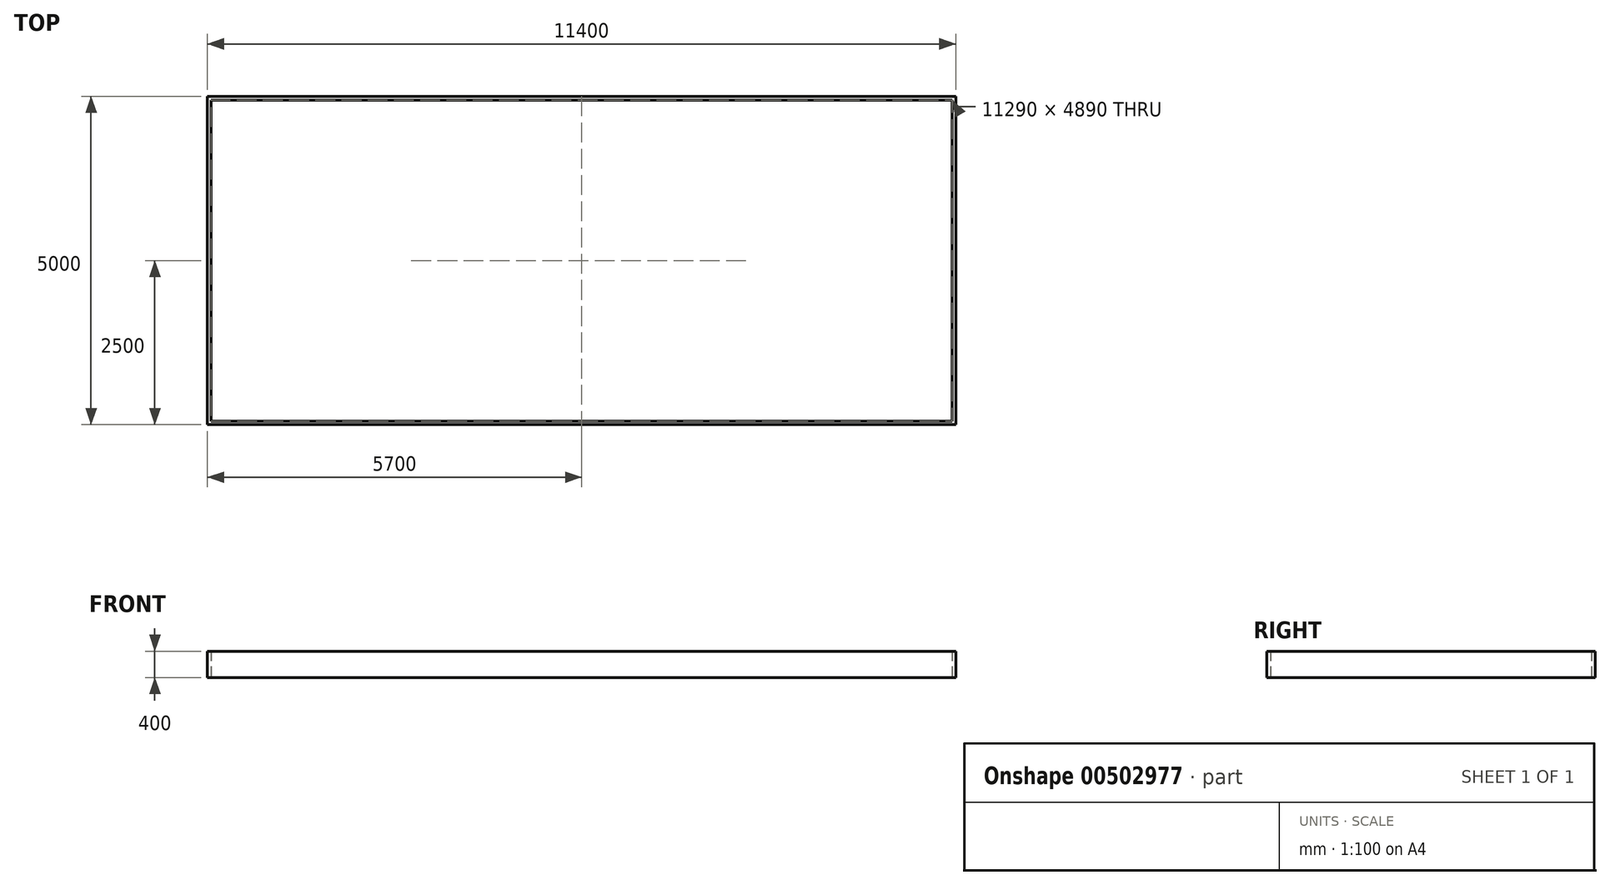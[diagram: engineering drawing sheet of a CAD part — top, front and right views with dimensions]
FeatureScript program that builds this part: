
annotation { "Feature Type Name" : "Feature", "Feature Type Description" : "" }
export const myFeature = defineFeature(function(context is Context, id is Id, definition is map)
    precondition{}
    {
        {
            var Q0;
            Q0=qCreatedBy(makeId("Top.planeOp"),FACE);
            var sketch = newSketch(context, id + "F0", { "sketchPlane" : qUnion([Q0])});
            skLineSegment(sketch, "E0.bottom", {"start": v(0, 0) * mm, "end": v(11400, 0) * mm});
            skLineSegment(sketch, "E0.top", {"start": v(0, -5000) * mm, "end": v(11400, -5000) * mm});
            skLineSegment(sketch, "E0.left", {"start": v(0, 0) * mm, "end": v(0, -5000) * mm});
            skLineSegment(sketch, "E0.right", {"start": v(11400, 0) * mm, "end": v(11400, -5000) * mm});
            skLineSegment(sketch, "E1.0", {"start": v(300, -300) * mm, "end": v(4550.61, -300) * mm});
            skLineSegment(sketch, "E1.1", {"start": v(300, -300) * mm, "end": v(300, -4700) * mm});
            skLineSegment(sketch, "E1.2", {"start": v(300, -4700) * mm, "end": v(4550.61, -4700) * mm});
            skLineSegment(sketch, "E1.3", {"start": v(11100, -300) * mm, "end": v(11100, -4700) * mm});
            skLineSegment(sketch, "E2.left", {"start": v(4550.61, -300) * mm, "end": v(4550.61, -4700) * mm});
            skLineSegment(sketch, "E2.right", {"start": v(4850.61, -300) * mm, "end": v(4850.61, -4700) * mm});
            skLineSegment(sketch, "E3.trimOffspring", {"start": v(4850.61, -4700) * mm, "end": v(11100, -4700) * mm});
            skLineSegment(sketch, "E4.trimOffspring", {"start": v(4850.61, -300) * mm, "end": v(11100, -300) * mm});
            skLineSegment(sketch, "E5.0", {"start": v(55, -55) * mm, "end": v(11345, -55) * mm});
            skLineSegment(sketch, "E5.1", {"start": v(55, -55) * mm, "end": v(55, -4945) * mm});
            skLineSegment(sketch, "E5.2", {"start": v(55, -4945) * mm, "end": v(11345, -4945) * mm});
            skLineSegment(sketch, "E5.3", {"start": v(11345, -55) * mm, "end": v(11345, -4945) * mm});
            skLineSegment(sketch, "E6.0", {"start": v(4795.61, -55) * mm, "end": v(4795.61, -4945) * mm});
            skLineSegment(sketch, "E7.0", {"start": v(200, -4800) * mm, "end": v(11200, -4800) * mm});
            skLineSegment(sketch, "E7.1", {"start": v(200, -200) * mm, "end": v(200, -4800) * mm});
            skLineSegment(sketch, "E7.2", {"start": v(200, -200) * mm, "end": v(11200, -200) * mm});
            skLineSegment(sketch, "E7.3", {"start": v(11200, -200) * mm, "end": v(11200, -4800) * mm});
            skLineSegment(sketch, "E8.0", {"start": v(4605.61, -55) * mm, "end": v(4605.61, -4945) * mm});
            skLineSegment(sketch, "E9.bottom", {"start": v(413.07, -515.85) * mm, "end": v(1913.07, -515.85) * mm});
            skLineSegment(sketch, "E9.top", {"start": v(413.07, -3515.85) * mm, "end": v(1913.07, -3515.85) * mm});
            skLineSegment(sketch, "E9.left", {"start": v(413.07, -515.85) * mm, "end": v(413.07, -3515.85) * mm});
            skLineSegment(sketch, "E9.right", {"start": v(1913.07, -515.85) * mm, "end": v(1913.07, -3515.85) * mm});
            skSolve(sketch);
        }
        {
            var Q0;
            Q0=makeQuery(id+"F0.imprint","IMPRINT",FACE,{"disambiguationData":[TD([[makeQuery(id+"F0.imprint","IMPRINT",EDGE,{"derivedFrom":sQuery(id+"F0.wireOp",EDGE,"E0.bottom")}),-1.0]])]});
            extrude(context, id + "F1", {"entities" : qUnion([Q0]), "depth" : 400 * mm});
        }
    });
